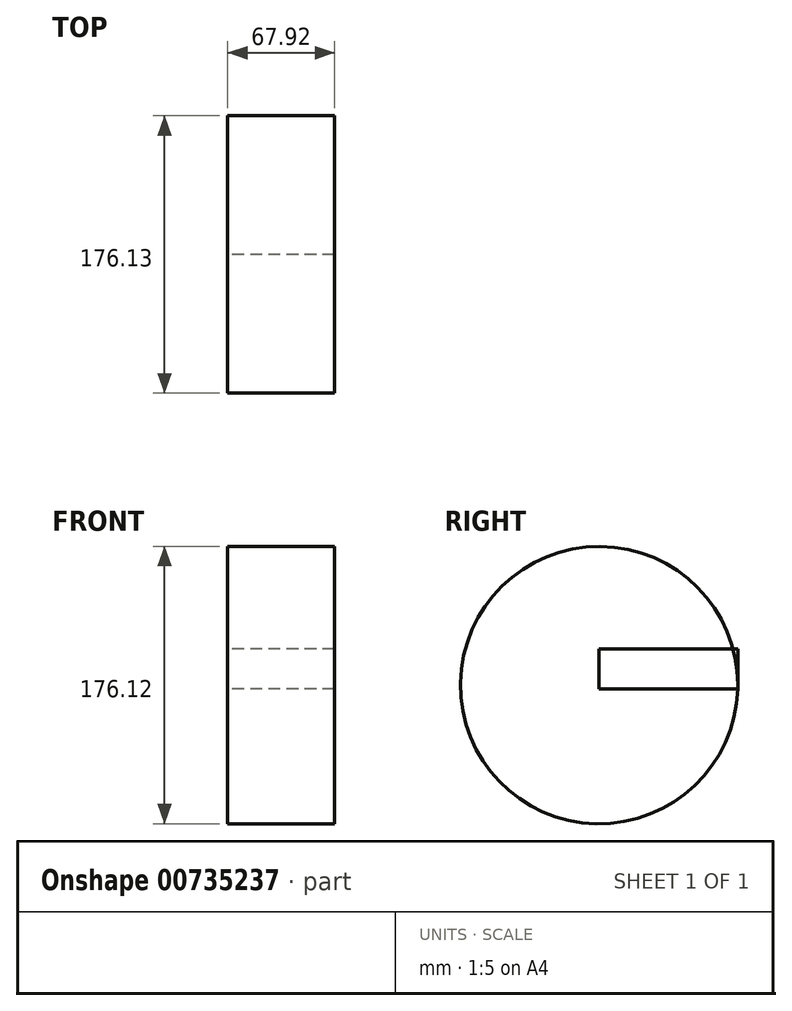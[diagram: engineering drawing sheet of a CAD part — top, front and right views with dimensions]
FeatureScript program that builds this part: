
annotation { "Feature Type Name" : "Feature", "Feature Type Description" : "" }
export const myFeature = defineFeature(function(context is Context, id is Id, definition is map)
    precondition{}
    {
        {
            var Q0;
            Q0=qCreatedBy(makeId("Top.planeOp"),FACE);
            var sketch = newSketch(context, id + "F0", { "sketchPlane" : qUnion([Q0])});
            skLineSegment(sketch, "E0.bottom", {"start": v(33.96, 44.03) * mm, "end": v(-33.96, 44.03) * mm});
            skLineSegment(sketch, "E0.top", {"start": v(33.96, -44.03) * mm, "end": v(-33.96, -44.03) * mm});
            skLineSegment(sketch, "E0.left", {"start": v(33.96, 44.03) * mm, "end": v(33.96, -44.03) * mm});
            skLineSegment(sketch, "E0.right", {"start": v(-33.96, 44.03) * mm, "end": v(-33.96, -44.03) * mm});
            skPoint(sketch, "E0.middle", {"position": v(0, 0) * mm});
            skSolve(sketch);
        }
        {
            var Q0;
            Q0=makeQuery(id+"F0.imprint","IMPRINT",FACE,{"disambiguationData":[TD([[makeQuery(id+"F0.imprint","IMPRINT",EDGE,{"derivedFrom":sQuery(id+"F0.wireOp",EDGE,"E0.bottom")}),1.0]])]});
            extrude(context, id + "F1", {"entities" : qUnion([Q0]), "depth" : 2.54 * mm, "offsetDistance" : 25.4 * mm});
        }
        {
            var Q0;
            Q0=makeQuery(id+"F1.opExtrude","CAP_FACE",FACE,{"disambiguationData":[OSD([sQuery(id+"F0.wireOp",EDGE,"E0.bottom"),sQuery(id+"F0.wireOp",EDGE,"E0.top"),sQuery(id+"F0.wireOp",EDGE,"E0.left"),sQuery(id+"F0.wireOp",EDGE,"E0.right")])],"isStart":false});
            var Q1;
            Q1=makeQuery(id+"F1.opExtrude","CAP_EDGE",EDGE,{"disambiguationData":[OSD([sQuery(id+"F0.wireOp",EDGE,"E0.top")])],"isStart":false});
            revolve(context, id + "F2", {"operationType" : NewBodyOperationType.ADD, "surfaceOperationType" : NewSurfaceOperationType.NEW, "entities" : qUnion([Q0]), "axis" : qUnion([Q1]), "revolveType" : RevolveType.FULL});
        }
        {
            var Q0;
            Q0=makeQuery(id+"F0.imprint","IMPRINT",FACE,{"disambiguationData":[TD([[makeQuery(id+"F0.imprint","IMPRINT",EDGE,{"derivedFrom":sQuery(id+"F0.wireOp",EDGE,"E0.bottom")}),1.0]])]});
            extrude(context, id + "F3", {"entities" : qUnion([Q0]), "depth" : 25.4 * mm});
        }
    });
